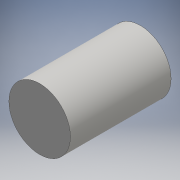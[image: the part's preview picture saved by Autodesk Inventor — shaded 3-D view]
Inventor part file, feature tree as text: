
AUTODESK INVENTOR PART (.ipt)
format: ipt  version: 2016 (Build 200138000, 138)  size: 86,528 bytes
history: native  units: mm
features: other x1, extrude x1, sketch x1
ambient origin geometry x8: Origin, YZ Plane, XZ Plane, XY Plane, X Axis, Y Axis, Z Axis, Center Point
bodies: Body1 (feature_tree)
feature tree (3):
  other  "ソリッド1"
  extrude  "押し出し1"  Depth=44.0mm
  sketch  "スケッチ1"
